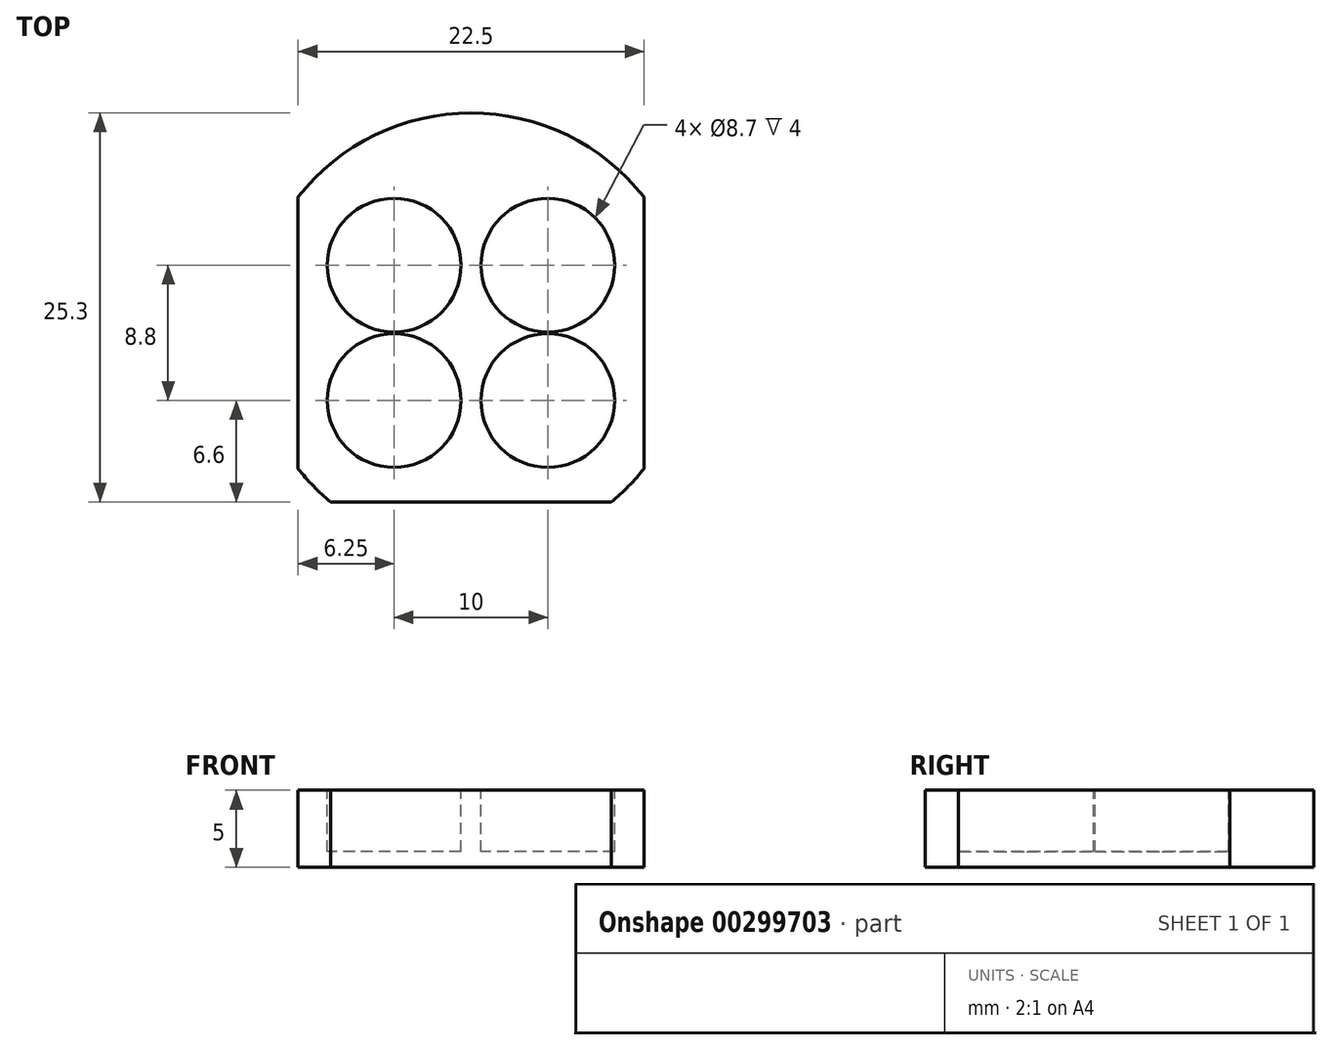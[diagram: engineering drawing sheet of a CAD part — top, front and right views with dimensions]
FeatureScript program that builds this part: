
annotation { "Feature Type Name" : "Feature", "Feature Type Description" : "" }
export const myFeature = defineFeature(function(context is Context, id is Id, definition is map)
    precondition{}
    {
        {
            var Q0;
            Q0=qCreatedBy(makeId("Top.planeOp"),FACE);
            var sketch = newSketch(context, id + "F0", { "sketchPlane" : qUnion([Q0])});
            skCircle(sketch, "E0", {"center": v(0, 0) * mm, "radius": 14.3 * mm});
            skSolve(sketch);
        }
        {
            var Q0;
            Q0 = qSketchRegion(id + "F0", true);
            extrude(context, id + "F1", {"entities" : qUnion([Q0]), "depth" : 5 * mm});
        }
        {
            var Q0;
            Q0=makeQuery(id+"F1.opExtrude","CAP_FACE",FACE,{"disambiguationData":[OSD([sQuery(id+"F0.wireOp",EDGE,"E0")])],"isStart":false});
            var sketch = newSketch(context, id + "F2", { "sketchPlane" : qUnion([Q0])});
            skLineSegment(sketch, "E1.bottom", {"start": v(5, -4.4) * mm, "end": v(-5, -4.4) * mm});
            skLineSegment(sketch, "E1.top", {"start": v(5, 4.4) * mm, "end": v(-5, 4.4) * mm});
            skLineSegment(sketch, "E1.left", {"start": v(5, -4.4) * mm, "end": v(5, 4.4) * mm});
            skLineSegment(sketch, "E1.right", {"start": v(-5, -4.4) * mm, "end": v(-5, 4.4) * mm});
            skPoint(sketch, "E1.middle", {"position": v(0, 0) * mm});
            skCircle(sketch, "E2", {"center": v(-5, 4.4) * mm, "radius": 4.35 * mm});
            skCircle(sketch, "E3", {"center": v(-5, -4.4) * mm, "radius": 4.35 * mm});
            skCircle(sketch, "E4", {"center": v(5, -4.4) * mm, "radius": 4.35 * mm});
            skCircle(sketch, "E5", {"center": v(5, 4.4) * mm, "radius": 4.35 * mm});
            skSolve(sketch);
        }
        {
            var Q0;
            {var subQ0=sQuery(id+"F2.wireOp",EDGE,"E1.left");var subQ1=sQuery(id+"F2.wireOp",EDGE,"E1.bottom");var subQ2=makeQuery(id+"F2.imprint","INTERSECT",VERTEX,{"derivedFrom":[subQ1,subQ0]});Q0=makeQuery(id+"F2.imprint","IMPRINT",FACE,{"disambiguationData":[TD([[makeQuery(id+"F2.imprint","IMPRINT",EDGE,{"disambiguationData":[TD([[subQ2,-1.0]])],"derivedFrom":subQ1}),-1.0]])]});}
            var Q1;
            {var subQ0=sQuery(id+"F2.wireOp",EDGE,"E1.left");var subQ1=sQuery(id+"F2.wireOp",EDGE,"E1.bottom");var subQ2=makeQuery(id+"F2.imprint","INTERSECT",VERTEX,{"derivedFrom":[subQ1,subQ0]});Q1=makeQuery(id+"F2.imprint","IMPRINT",FACE,{"disambiguationData":[TD([[makeQuery(id+"F2.imprint","IMPRINT",EDGE,{"disambiguationData":[TD([[subQ2,-1.0]])],"derivedFrom":subQ1}),1.0]])]});}
            var Q2;
            {var subQ0=sQuery(id+"F2.wireOp",EDGE,"E1.right");var subQ1=sQuery(id+"F2.wireOp",EDGE,"E1.bottom");var subQ2=makeQuery(id+"F2.imprint","INTERSECT",VERTEX,{"derivedFrom":[subQ1,subQ0]});Q2=makeQuery(id+"F2.imprint","IMPRINT",FACE,{"disambiguationData":[TD([[makeQuery(id+"F2.imprint","IMPRINT",EDGE,{"disambiguationData":[TD([[subQ2,1.0]])],"derivedFrom":subQ1}),-1.0]])]});}
            var Q3;
            {var subQ0=sQuery(id+"F2.wireOp",EDGE,"E1.right");var subQ1=sQuery(id+"F2.wireOp",EDGE,"E1.bottom");var subQ2=makeQuery(id+"F2.imprint","INTERSECT",VERTEX,{"derivedFrom":[subQ1,subQ0]});Q3=makeQuery(id+"F2.imprint","IMPRINT",FACE,{"disambiguationData":[TD([[makeQuery(id+"F2.imprint","IMPRINT",EDGE,{"disambiguationData":[TD([[subQ2,1.0]])],"derivedFrom":subQ1}),1.0]])]});}
            var Q4;
            {var subQ0=sQuery(id+"F2.wireOp",EDGE,"E1.left");var subQ1=sQuery(id+"F2.wireOp",EDGE,"E1.top");var subQ2=makeQuery(id+"F2.imprint","INTERSECT",VERTEX,{"derivedFrom":[subQ1,subQ0]});Q4=makeQuery(id+"F2.imprint","IMPRINT",FACE,{"disambiguationData":[TD([[makeQuery(id+"F2.imprint","IMPRINT",EDGE,{"disambiguationData":[TD([[subQ2,-1.0]])],"derivedFrom":subQ1}),1.0]])]});}
            var Q5;
            {var subQ0=sQuery(id+"F2.wireOp",EDGE,"E1.left");var subQ1=sQuery(id+"F2.wireOp",EDGE,"E1.top");var subQ2=makeQuery(id+"F2.imprint","INTERSECT",VERTEX,{"derivedFrom":[subQ1,subQ0]});Q5=makeQuery(id+"F2.imprint","IMPRINT",FACE,{"disambiguationData":[TD([[makeQuery(id+"F2.imprint","IMPRINT",EDGE,{"disambiguationData":[TD([[subQ2,-1.0]])],"derivedFrom":subQ1}),-1.0]])]});}
            var Q6;
            {var subQ0=sQuery(id+"F2.wireOp",EDGE,"E1.right");var subQ1=sQuery(id+"F2.wireOp",EDGE,"E1.top");var subQ2=makeQuery(id+"F2.imprint","INTERSECT",VERTEX,{"derivedFrom":[subQ1,subQ0]});Q6=makeQuery(id+"F2.imprint","IMPRINT",FACE,{"disambiguationData":[TD([[makeQuery(id+"F2.imprint","IMPRINT",EDGE,{"disambiguationData":[TD([[subQ2,1.0]])],"derivedFrom":subQ1}),-1.0]])]});}
            var Q7;
            {var subQ0=sQuery(id+"F2.wireOp",EDGE,"E1.right");var subQ1=sQuery(id+"F2.wireOp",EDGE,"E1.top");var subQ2=makeQuery(id+"F2.imprint","INTERSECT",VERTEX,{"derivedFrom":[subQ1,subQ0]});Q7=makeQuery(id+"F2.imprint","IMPRINT",FACE,{"disambiguationData":[TD([[makeQuery(id+"F2.imprint","IMPRINT",EDGE,{"disambiguationData":[TD([[subQ2,1.0]])],"derivedFrom":subQ1}),1.0]])]});}
            extrude(context, id + "F3", {"entities" : qUnion([Q0, Q1, Q2, Q3, Q4, Q5, Q6, Q7]), "operationType" : NewBodyOperationType.REMOVE, "oppositeDirection" : true, "depth" : 4 * mm});
        }
        {
            var Q0;
            Q0=makeQuery(id+"F1.opExtrude","CAP_FACE",FACE,{"disambiguationData":[OSD([sQuery(id+"F0.wireOp",EDGE,"E0")])],"isStart":false});
            var sketch = newSketch(context, id + "F4", { "sketchPlane" : qUnion([Q0])});
            skLineSegment(sketch, "E6.bottom", {"start": v(11.25, -11) * mm, "end": v(-11.25, -11) * mm});
            skLineSegment(sketch, "E6.top", {"start": v(11.25, 11) * mm, "end": v(-11.25, 11) * mm});
            skLineSegment(sketch, "E6.left", {"start": v(11.25, -11) * mm, "end": v(11.25, 11) * mm});
            skLineSegment(sketch, "E6.right", {"start": v(-11.25, -11) * mm, "end": v(-11.25, 11) * mm});
            skPoint(sketch, "E6.middle", {"position": v(0, 0) * mm});
            skSolve(sketch);
        }
        {
            var Q0;
            {var subQ0=sQuery(id+"F4.wireOp",EDGE,"E6.right");var subQ1=makeQuery(id+"F1.opExtrude","CAP_EDGE",EDGE,{"disambiguationData":[OSD([sQuery(id+"F0.wireOp",EDGE,"E0")])],"isStart":false});var subQ2=makeQuery(id+"F4.imprint","INTERSECT",VERTEX,{"disambiguationData":[OD(0.0)],"derivedFrom":[subQ1,subQ0]});Q0=makeQuery(id+"F4.imprint","IMPRINT",FACE,{"disambiguationData":[TD([[makeQuery(id+"F4.imprint","IMPRINT",EDGE,{"disambiguationData":[TD([[subQ2,-1.0]])],"derivedFrom":subQ0}),1.0]])]});}
            var Q1;
            {var subQ0=sQuery(id+"F4.wireOp",EDGE,"E6.left");var subQ1=makeQuery(id+"F1.opExtrude","CAP_EDGE",EDGE,{"disambiguationData":[OSD([sQuery(id+"F0.wireOp",EDGE,"E0")])],"isStart":false});var subQ2=makeQuery(id+"F4.imprint","INTERSECT",VERTEX,{"disambiguationData":[OD(0.0)],"derivedFrom":[subQ1,subQ0]});Q1=makeQuery(id+"F4.imprint","IMPRINT",FACE,{"disambiguationData":[TD([[makeQuery(id+"F4.imprint","IMPRINT",EDGE,{"disambiguationData":[TD([[subQ2,-1.0]])],"derivedFrom":subQ0}),-1.0]])]});}
            var Q2;
            {var subQ0=sQuery(id+"F4.wireOp",EDGE,"E6.bottom");var subQ1=makeQuery(id+"F1.opExtrude","CAP_EDGE",EDGE,{"disambiguationData":[OSD([sQuery(id+"F0.wireOp",EDGE,"E0")])],"isStart":false});var subQ2=makeQuery(id+"F4.imprint","INTERSECT",VERTEX,{"disambiguationData":[OD(0.0)],"derivedFrom":[subQ1,subQ0]});Q2=makeQuery(id+"F4.imprint","IMPRINT",FACE,{"disambiguationData":[TD([[makeQuery(id+"F4.imprint","IMPRINT",EDGE,{"disambiguationData":[TD([[subQ2,-1.0]])],"derivedFrom":subQ0}),1.0]])]});}
            extrude(context, id + "F5", {"entities" : qUnion([Q0, Q1, Q2]), "operationType" : NewBodyOperationType.REMOVE, "oppositeDirection" : true, "depth" : 25 * mm});
        }
    });
